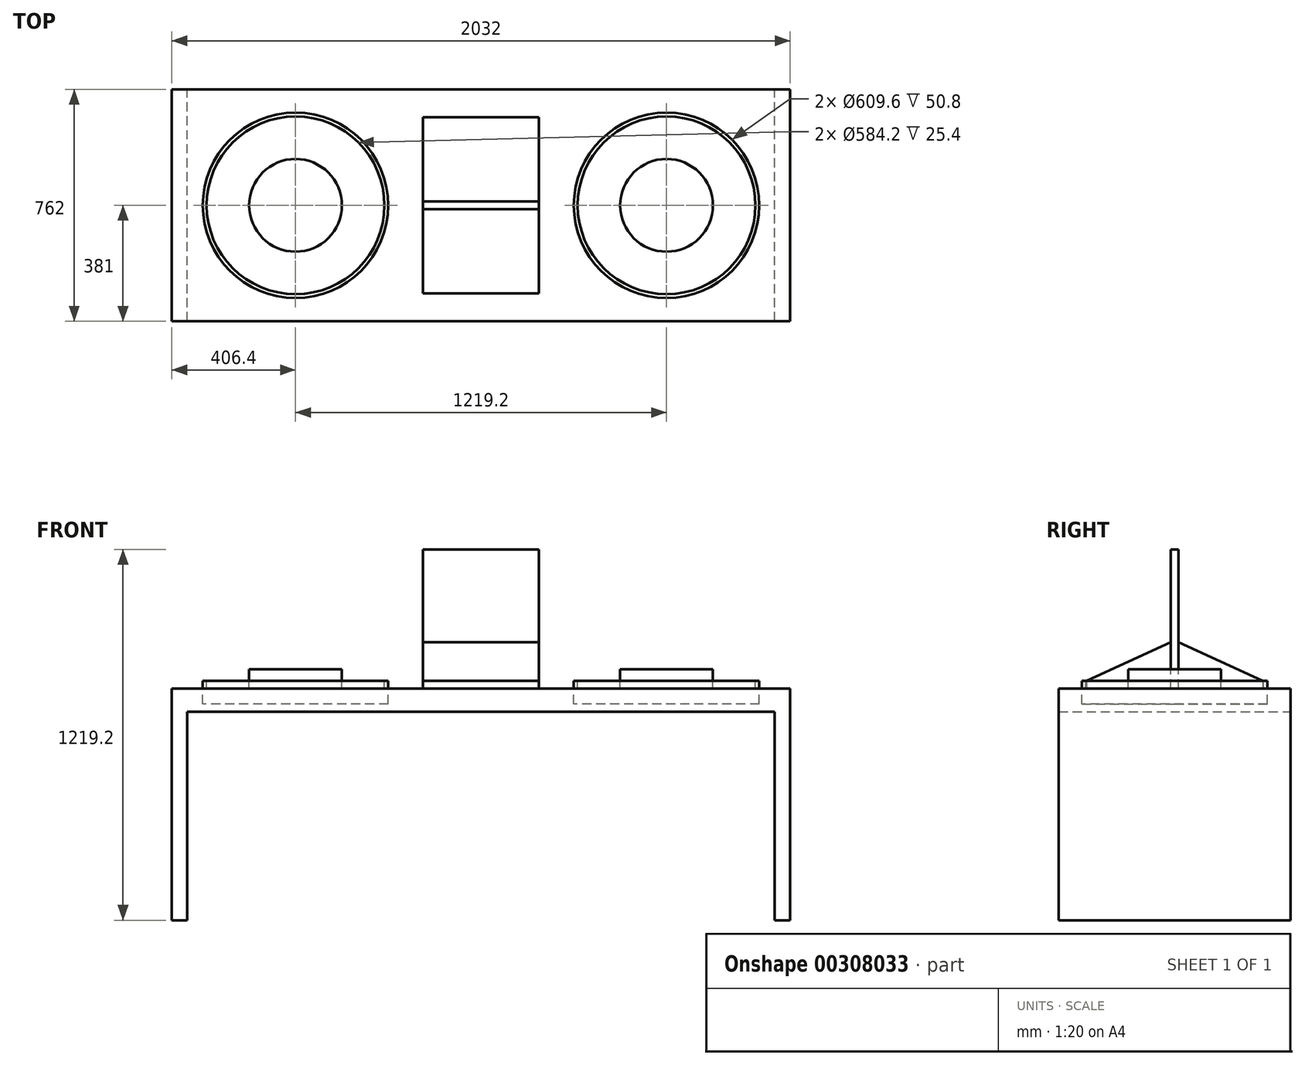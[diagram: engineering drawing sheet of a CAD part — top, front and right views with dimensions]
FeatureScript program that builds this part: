
annotation { "Feature Type Name" : "Feature", "Feature Type Description" : "" }
export const myFeature = defineFeature(function(context is Context, id is Id, definition is map)
    precondition{}
    {
        {
            var Q0;
            Q0=qCreatedBy(makeId("Top.planeOp"),FACE);
            var sketch = newSketch(context, id + "F0", { "sketchPlane" : qUnion([Q0])});
            skLineSegment(sketch, "E0.bottom", {"start": v(-1016, 381) * mm, "end": v(1016, 381) * mm});
            skLineSegment(sketch, "E0.top", {"start": v(-1016, -381) * mm, "end": v(1016, -381) * mm});
            skLineSegment(sketch, "E0.left", {"start": v(-1016, 381) * mm, "end": v(-1016, -381) * mm});
            skLineSegment(sketch, "E0.right", {"start": v(1016, 381) * mm, "end": v(1016, -381) * mm});
            skPoint(sketch, "E0.middle", {"position": v(0, 0) * mm});
            skSolve(sketch);
        }
        {
            var Q0;
            Q0=makeQuery(id+"F0.imprint","IMPRINT",FACE,{"disambiguationData":[TD([[makeQuery(id+"F0.imprint","IMPRINT",EDGE,{"derivedFrom":sQuery(id+"F0.wireOp",EDGE,"E0.bottom")}),-1.0]])]});
            extrude(context, id + "F1", {"entities" : qUnion([Q0]), "oppositeDirection" : true, "depth" : 76.2 * mm});
        }
        {
            var Q0;
            Q0=makeQuery(id+"F1.opExtrude","CAP_FACE",FACE,{"disambiguationData":[OSD([sQuery(id+"F0.wireOp",EDGE,"E0.bottom"),sQuery(id+"F0.wireOp",EDGE,"E0.top"),sQuery(id+"F0.wireOp",EDGE,"E0.left"),sQuery(id+"F0.wireOp",EDGE,"E0.right")])],"isStart":false});
            var sketch = newSketch(context, id + "F2", { "sketchPlane" : qUnion([Q0])});
            skLineSegment(sketch, "E1.bottom", {"start": v(-1016, 381) * mm, "end": v(-965.2, 381) * mm});
            skLineSegment(sketch, "E1.top", {"start": v(-1016, -381) * mm, "end": v(-965.2, -381) * mm});
            skLineSegment(sketch, "E1.left", {"start": v(-1016, 381) * mm, "end": v(-1016, -381) * mm});
            skLineSegment(sketch, "E1.right", {"start": v(-965.2, 381) * mm, "end": v(-965.2, -381) * mm});
            skLineSegment(sketch, "E2.bottom", {"start": v(1016, 381) * mm, "end": v(965.2, 381) * mm});
            skLineSegment(sketch, "E2.top", {"start": v(1016, -381) * mm, "end": v(965.2, -381) * mm});
            skLineSegment(sketch, "E2.left", {"start": v(1016, 381) * mm, "end": v(1016, -381) * mm});
            skLineSegment(sketch, "E2.right", {"start": v(965.2, 381) * mm, "end": v(965.2, -381) * mm});
            skSolve(sketch);
        }
        {
            var Q0;
            Q0 = qSketchRegion(id + "F2", true);
            extrude(context, id + "F3", {"entities" : qUnion([Q0]), "operationType" : NewBodyOperationType.ADD, "depth" : 685.8 * mm});
        }
        {
            var Q0;
            Q0=qCreatedBy(makeId("Front.planeOp"),FACE);
            var sketch = newSketch(context, id + "F4", { "sketchPlane" : qUnion([Q0])});
            skLineSegment(sketch, "E3", {"start": v(-609.6, -50.8) * mm, "end": v(-914.4, -50.8) * mm});
            skLineSegment(sketch, "E4", {"start": v(-914.4, -50.8) * mm, "end": v(-914.4, 25.4) * mm});
            skLineSegment(sketch, "E5", {"start": v(-914.4, 25.4) * mm, "end": v(-901.7, 25.4) * mm});
            skLineSegment(sketch, "E6", {"start": v(-901.7, 25.4) * mm, "end": v(-901.7, -38.1) * mm});
            skLineSegment(sketch, "E7", {"start": v(-901.7, -38.1) * mm, "end": v(-609.6, -38.1) * mm});
            skLineSegment(sketch, "E8", {"start": v(-609.6, -38.1) * mm, "end": v(-609.6, -50.8) * mm});
            skSolve(sketch);
        }
        {
            var Q0;
            Q0=makeQuery(id+"F4.imprint","IMPRINT",FACE,{"disambiguationData":[TD([[makeQuery(id+"F4.imprint","IMPRINT",EDGE,{"derivedFrom":sQuery(id+"F4.wireOp",EDGE,"E3")}),-1.0]])]});
            var Q1;
            Q1=sQuery(id+"F4.wireOp",EDGE,"E8");
            revolve(context, id + "F5", {"entities" : qUnion([Q0]), "axis" : qUnion([Q1]), "revolveType" : RevolveType.FULL});
        }
        {
            var Q0;
            Q0=qCreatedBy(makeId("Front.planeOp"),FACE);
            var sketch = newSketch(context, id + "F6", { "sketchPlane" : qUnion([Q0])});
            skLineSegment(sketch, "E9", {"start": v(-609.6, 63.5) * mm, "end": v(-609.6, -38.1) * mm});
            skLineSegment(sketch, "E10", {"start": v(-609.6, -38.1) * mm, "end": v(-762, -38.1) * mm});
            skLineSegment(sketch, "E11", {"start": v(-762, -38.1) * mm, "end": v(-762, 63.5) * mm});
            skLineSegment(sketch, "E12", {"start": v(-762, 63.5) * mm, "end": v(-609.6, 63.5) * mm});
            skSolve(sketch);
        }
        {
            var Q0;
            Q0=makeQuery(id+"F6.imprint","IMPRINT",FACE,{"disambiguationData":[TD([[makeQuery(id+"F6.imprint","IMPRINT",EDGE,{"derivedFrom":sQuery(id+"F6.wireOp",EDGE,"E9")}),-1.0]])]});
            var Q1;
            Q1=sQuery(id+"F6.wireOp",EDGE,"E9");
            revolve(context, id + "F7", {"entities" : qUnion([Q0]), "axis" : qUnion([Q1]), "revolveType" : RevolveType.FULL});
        }
        {
            var Q0;
            Q0=makeQuery(id+"F7.opRevolve","SWEPT_BODY",BODY,{"disambiguationData":[OSD([sQuery(id+"F6.wireOp",EDGE,"E9"),sQuery(id+"F6.wireOp",EDGE,"E10"),sQuery(id+"F6.wireOp",EDGE,"E11"),sQuery(id+"F6.wireOp",EDGE,"E12")])]});
            var Q1;
            Q1=makeQuery(id+"F5.opRevolve","SWEPT_BODY",BODY,{"disambiguationData":[OSD([sQuery(id+"F4.wireOp",EDGE,"E3"),sQuery(id+"F4.wireOp",EDGE,"E4"),sQuery(id+"F4.wireOp",EDGE,"E5"),sQuery(id+"F4.wireOp",EDGE,"E6"),sQuery(id+"F4.wireOp",EDGE,"E7"),sQuery(id+"F4.wireOp",EDGE,"E8")])]});
            var Q2;
            Q2=qCreatedBy(makeId("Right.planeOp"),FACE);
            mirror(context, id + "F8", {"entities" : qUnion([Q0, Q1]), "mirrorPlane" : qUnion([Q2])});
        }
        {
            var Q0;
            Q0=qCreatedBy(makeId("Right.planeOp"),FACE);
            var sketch = newSketch(context, id + "F9", { "sketchPlane" : qUnion([Q0])});
            skLineSegment(sketch, "E13", {"start": v(0, 152.4) * mm, "end": v(-50.8, 152.4) * mm});
            skLineSegment(sketch, "E14", {"start": v(-50.8, 152.4) * mm, "end": v(-327.88, 25.4) * mm});
            skLineSegment(sketch, "E15", {"start": v(327.88, 25.4) * mm, "end": v(50.8, 152.4) * mm});
            skLineSegment(sketch, "E16", {"start": v(50.8, 152.4) * mm, "end": v(0, 152.4) * mm});
            skPoint(sketch, "E17.end.orphan", {"position": v(0.64, 25.4) * mm});
            skLineSegment(sketch, "E18", {"start": v(327.88, 25.4) * mm, "end": v(327.88, 0) * mm});
            skLineSegment(sketch, "E19", {"start": v(327.88, 0) * mm, "end": v(0, 0) * mm});
            skLineSegment(sketch, "E20", {"start": v(0, 0) * mm, "end": v(-327.88, 0) * mm});
            skLineSegment(sketch, "E21", {"start": v(-327.88, 0) * mm, "end": v(-327.88, 25.4) * mm});
            skSolve(sketch);
        }
        {
            var Q0;
            Q0=makeQuery(id+"F9.imprint","IMPRINT",FACE,{"disambiguationData":[TD([[makeQuery(id+"F9.imprint","IMPRINT",EDGE,{"derivedFrom":sQuery(id+"F9.wireOp",EDGE,"E13")}),1.0]])]});
            extrude(context, id + "F10", {"entities" : qUnion([Q0]), "depth" : 127 * mm, "hasSecondDirection" : true, "secondDirectionOppositeDirection" : true, "secondDirectionDepth" : 127 * mm});
        }
        {
            var Q0;
            Q0=makeQuery(id+"F1.opExtrude","CAP_FACE",FACE,{"disambiguationData":[OSD([sQuery(id+"F0.wireOp",EDGE,"E0.bottom"),sQuery(id+"F0.wireOp",EDGE,"E0.top"),sQuery(id+"F0.wireOp",EDGE,"E0.left"),sQuery(id+"F0.wireOp",EDGE,"E0.right")])],"isStart":true});
            var sketch = newSketch(context, id + "F11", { "sketchPlane" : qUnion([Q0])});
            skCircle(sketch, "E22.0", {"center": v(-609.6, 0) * mm, "radius": 304.8 * mm});
            skCircle(sketch, "E23.0", {"center": v(609.6, 0) * mm, "radius": 304.8 * mm});
            skSolve(sketch);
        }
        {
            var Q0;
            Q0 = qSketchRegion(id + "F11", true);
            extrude(context, id + "F12", {"entities" : qUnion([Q0]), "operationType" : NewBodyOperationType.REMOVE, "oppositeDirection" : true, "depth" : 50.8 * mm});
        }
        {
            var Q0;
            Q0=qCreatedBy(makeId("Front.planeOp"),FACE);
            var sketch = newSketch(context, id + "F13", { "sketchPlane" : qUnion([Q0])});
            skLineSegment(sketch, "E24", {"start": v(-622.3, 63.5) * mm, "end": v(-622.3, 350.52) * mm});
            skFitSpline(sketch, "E25", {"points": [v(-622.3, 350.52) * mm, v(-549.47, 317.89) * mm, v(-525.4, 252.33) * mm, v(-554.03, 131.76) * mm, v(-577.7, 63.5) * mm], "startDerivative": vector(441.6, -9.7) * mm, "endDerivative": vector(7.65, -319.24) * mm});
            skLineSegment(sketch, "E26", {"start": v(-622.3, 63.5) * mm, "end": v(-577.7, 63.5) * mm});
            skSolve(sketch);
        }
        {
            var Q0;
            Q0=makeQuery(id+"F10.opExtrude","SWEPT_BODY",BODY,{"disambiguationData":[OSD([sQuery(id+"F9.wireOp",EDGE,"E13"),sQuery(id+"F9.wireOp",EDGE,"E14"),sQuery(id+"F9.wireOp",EDGE,"E15"),sQuery(id+"F9.wireOp",EDGE,"E16"),sQuery(id+"F9.wireOp",EDGE,"E18"),sQuery(id+"F9.wireOp",EDGE,"E19"),sQuery(id+"F9.wireOp",EDGE,"E20"),sQuery(id+"F9.wireOp",EDGE,"E21")])]});
            deleteBodies(context, id + "F14", {"entities" : qUnion([Q0])});
        }
        {
            var Q0;
            Q0=qCreatedBy(makeId("Front.planeOp"),FACE);
            var sketch = newSketch(context, id + "F15", { "sketchPlane" : qUnion([Q0])});
            skLineSegment(sketch, "E27", {"start": v(-203.2, 0) * mm, "end": v(-203.2, 457.2) * mm});
            skLineSegment(sketch, "E28", {"start": v(-203.2, 457.2) * mm, "end": v(0, 457.2) * mm});
            skLineSegment(sketch, "E29", {"start": v(0, 457.2) * mm, "end": v(0, 431.8) * mm});
            skLineSegment(sketch, "E30", {"start": v(0, 431.8) * mm, "end": v(-177.8, 431.8) * mm});
            skLineSegment(sketch, "E31", {"start": v(-177.8, 431.8) * mm, "end": v(-177.8, 25.4) * mm});
            skLineSegment(sketch, "E32", {"start": v(-177.8, 0) * mm, "end": v(-203.2, 0) * mm});
            skLineSegment(sketch, "E33", {"start": v(0, 261.79) * mm, "end": v(0, 156.56) * mm, "construction": true});
            skLineSegment(sketch, "E34.MirrorCS", {"start": v(0, 431.8) * mm, "end": v(177.8, 431.8) * mm});
            skLineSegment(sketch, "E35.MirrorCS", {"start": v(203.2, 457.2) * mm, "end": v(0, 457.2) * mm});
            skLineSegment(sketch, "E36.MirrorCS", {"start": v(177.8, 0) * mm, "end": v(203.2, 0) * mm});
            skLineSegment(sketch, "E37", {"start": v(-177.8, 0) * mm, "end": v(0, 0) * mm});
            skLineSegment(sketch, "E38", {"start": v(0, 0) * mm, "end": v(0, 25.4) * mm});
            skLineSegment(sketch, "E39", {"start": v(0, 25.4) * mm, "end": v(-177.8, 25.4) * mm});
            skPoint(sketch, "E40.MirrorCS.end.orphan", {"position": v(177.8, 0) * mm});
            skPoint(sketch, "E41.MirrorCS.start.orphan", {"position": v(203.2, 0) * mm});
            skLineSegment(sketch, "E42.MirrorCS", {"start": v(203.2, 0) * mm, "end": v(203.2, 457.2) * mm});
            skLineSegment(sketch, "E43.MirrorCS", {"start": v(177.8, 431.8) * mm, "end": v(177.8, 25.4) * mm});
            skLineSegment(sketch, "E44.MirrorCS", {"start": v(0, 25.4) * mm, "end": v(177.8, 25.4) * mm});
            skLineSegment(sketch, "E45.MirrorCS", {"start": v(177.8, 0) * mm, "end": v(0, 0) * mm});
            skSolve(sketch);
        }
        {
            var Q0;
            Q0 = qSketchRegion(id + "F15", true);
            extrude(context, id + "F16", {"entities" : qUnion([Q0]), "depth" : 12.7 * mm, "hasSecondDirection" : true, "secondDirectionOppositeDirection" : true, "secondDirectionDepth" : 12.7 * mm});
        }
        {
            var Q0;
            Q0=qCreatedBy(makeId("Front.planeOp"),FACE);
            var sketch = newSketch(context, id + "F17", { "sketchPlane" : qUnion([Q0])});
            skLineSegment(sketch, "E46.bottom", {"start": v(-177.8, 431.8) * mm, "end": v(177.8, 431.8) * mm});
            skLineSegment(sketch, "E46.top", {"start": v(-177.8, 0) * mm, "end": v(177.8, 0) * mm});
            skLineSegment(sketch, "E46.left", {"start": v(-177.8, 431.8) * mm, "end": v(-177.8, 0) * mm});
            skLineSegment(sketch, "E46.right", {"start": v(177.8, 431.8) * mm, "end": v(177.8, 0) * mm});
            skSolve(sketch);
        }
        {
            var Q0;
            Q0=makeQuery(id+"F17.imprint","IMPRINT",FACE,{"disambiguationData":[TD([[makeQuery(id+"F17.imprint","IMPRINT",EDGE,{"derivedFrom":sQuery(id+"F17.wireOp",EDGE,"E46.bottom")}),-1.0]])]});
            extrude(context, id + "F18", {"entities" : qUnion([Q0]), "depth" : 6.35 * mm, "hasSecondDirection" : true, "secondDirectionOppositeDirection" : true, "secondDirectionDepth" : 6.35 * mm});
        }
        {
            var Q0;
            Q0=makeQuery(id+"F16.opExtrude","SWEPT_BODY",BODY,{"disambiguationData":[OSD([sQuery(id+"F15.wireOp",EDGE,"E27"),sQuery(id+"F15.wireOp",EDGE,"E28"),sQuery(id+"F15.wireOp",EDGE,"E30"),sQuery(id+"F15.wireOp",EDGE,"E31"),sQuery(id+"F15.wireOp",EDGE,"E32"),sQuery(id+"F15.wireOp",EDGE,"E34.MirrorCS"),sQuery(id+"F15.wireOp",EDGE,"E35.MirrorCS"),sQuery(id+"F15.wireOp",EDGE,"E37"),sQuery(id+"F15.wireOp",EDGE,"E39"),sQuery(id+"F15.wireOp",EDGE,"E42.MirrorCS"),sQuery(id+"F15.wireOp",EDGE,"E43.MirrorCS"),sQuery(id+"F15.wireOp",EDGE,"E44.MirrorCS"),sQuery(id+"F15.wireOp",EDGE,"E45.MirrorCS"),sQuery(id+"F15.wireOp",EDGE,"E36.MirrorCS")])]});
            deleteBodies(context, id + "F19", {"entities" : qUnion([Q0])});
        }
        {
            var Q0;
            Q0=makeQuery(id+"F18.opExtrude","SWEPT_BODY",BODY,{"disambiguationData":[OSD([sQuery(id+"F17.wireOp",EDGE,"E46.bottom"),sQuery(id+"F17.wireOp",EDGE,"E46.top"),sQuery(id+"F17.wireOp",EDGE,"E46.left"),sQuery(id+"F17.wireOp",EDGE,"E46.right")])]});
            deleteBodies(context, id + "F20", {"entities" : qUnion([Q0])});
        }
        {
            var Q0;
            Q0=qCreatedBy(makeId("Front.planeOp"),FACE);
            var sketch = newSketch(context, id + "F21", { "sketchPlane" : qUnion([Q0])});
            skLineSegment(sketch, "E47.bottom", {"start": v(190.5, 0) * mm, "end": v(-190.5, 0) * mm});
            skLineSegment(sketch, "E47.top", {"start": v(190.5, 457.2) * mm, "end": v(-190.5, 457.2) * mm});
            skLineSegment(sketch, "E47.left", {"start": v(190.5, 0) * mm, "end": v(190.5, 457.2) * mm});
            skLineSegment(sketch, "E47.right", {"start": v(-190.5, 0) * mm, "end": v(-190.5, 457.2) * mm});
            skPoint(sketch, "E47.middle", {"position": v(0, 228.6) * mm});
            skSolve(sketch);
        }
        {
            var Q0;
            Q0=makeQuery(id+"F21.imprint","IMPRINT",FACE,{"disambiguationData":[TD([[makeQuery(id+"F21.imprint","IMPRINT",EDGE,{"derivedFrom":sQuery(id+"F21.wireOp",EDGE,"E47.bottom")}),-1.0]])]});
            extrude(context, id + "F22", {"entities" : qUnion([Q0]), "depth" : 12.7 * mm, "hasSecondDirection" : true, "secondDirectionOppositeDirection" : true, "secondDirectionDepth" : 12.7 * mm});
        }
        {
            var Q0;
            Q0=qCreatedBy(makeId("Right.planeOp"),FACE);
            var sketch = newSketch(context, id + "F23", { "sketchPlane" : qUnion([Q0])});
            skLineSegment(sketch, "E48", {"start": v(-12.7, 152.4) * mm, "end": v(-289.78, 25.4) * mm});
            skLineSegment(sketch, "E49", {"start": v(-12.7, 0) * mm, "end": v(-12.7, 152.4) * mm});
            skLineSegment(sketch, "E50", {"start": v(0, 248.59) * mm, "end": v(0, 0) * mm, "construction": true});
            skLineSegment(sketch, "E51.MirrorCS", {"start": v(12.7, 152.4) * mm, "end": v(289.78, 25.4) * mm});
            skLineSegment(sketch, "E52.MirrorCS", {"start": v(12.7, 0) * mm, "end": v(12.7, 152.4) * mm});
            skLineSegment(sketch, "E53", {"start": v(-289.78, 25.4) * mm, "end": v(-289.78, 0) * mm});
            skLineSegment(sketch, "E54", {"start": v(-289.78, 0) * mm, "end": v(-12.7, 0) * mm});
            skPoint(sketch, "E55.MirrorCS.end.orphan", {"position": v(12.7, 0) * mm});
            skPoint(sketch, "E55.MirrorCS.start.orphan", {"position": v(289.78, 25.4) * mm});
            skLineSegment(sketch, "E56.MirrorCS", {"start": v(289.78, 0) * mm, "end": v(12.7, 0) * mm});
            skLineSegment(sketch, "E57.MirrorCS", {"start": v(289.78, 25.4) * mm, "end": v(289.78, 0) * mm});
            skSolve(sketch);
        }
        {
            var Q0;
            Q0=makeQuery(id+"F23.imprint","IMPRINT",FACE,{"disambiguationData":[TD([[makeQuery(id+"F23.imprint","IMPRINT",EDGE,{"derivedFrom":sQuery(id+"F23.wireOp",EDGE,"E51.MirrorCS")}),-1.0]])]});
            var Q1;
            Q1=makeQuery(id+"F23.imprint","IMPRINT",FACE,{"disambiguationData":[TD([[makeQuery(id+"F23.imprint","IMPRINT",EDGE,{"derivedFrom":sQuery(id+"F23.wireOp",EDGE,"E48")}),1.0]])]});
            extrude(context, id + "F24", {"entities" : qUnion([Q0, Q1]), "depth" : 190.5 * mm, "hasSecondDirection" : true, "secondDirectionOppositeDirection" : true, "secondDirectionDepth" : 190.5 * mm});
        }
    });
